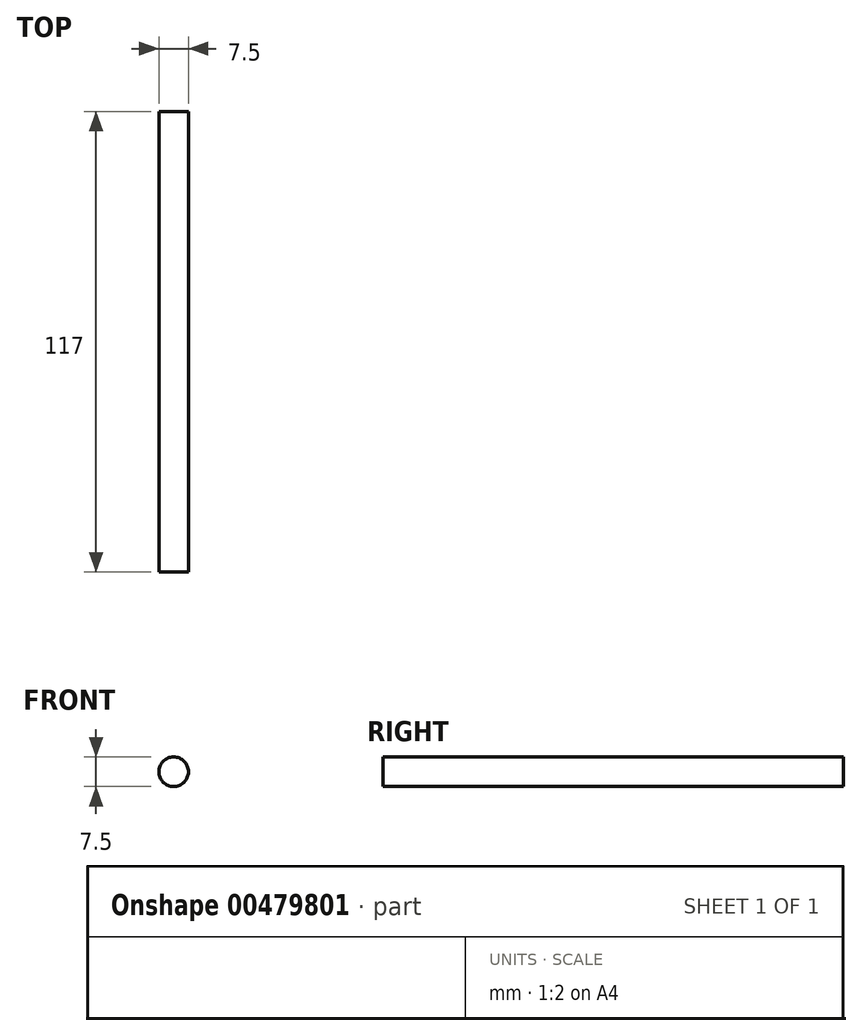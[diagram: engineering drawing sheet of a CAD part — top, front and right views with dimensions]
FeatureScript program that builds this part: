
annotation { "Feature Type Name" : "Feature", "Feature Type Description" : "" }
export const myFeature = defineFeature(function(context is Context, id is Id, definition is map)
    precondition{}
    {
        {
            var Q0;
            Q0=qCreatedBy(makeId("Front.planeOp"),FACE);
            var sketch = newSketch(context, id + "F0", { "sketchPlane" : qUnion([Q0])});
            skCircle(sketch, "E0", {"center": v(0, 0) * mm, "radius": 3.75 * mm});
            skSolve(sketch);
        }
        {
            var Q0;
            Q0=makeQuery(id+"F0.imprint","IMPRINT",FACE,{"disambiguationData":[TD([[makeQuery(id+"F0.imprint","IMPRINT",EDGE,{"derivedFrom":sQuery(id+"F0.wireOp",EDGE,"E0")}),1.0]])]});
            var Q1;
            Q1=sQuery(id+"F0.wireOp",EDGE,"E0");
            extrude(context, id + "F1", {"entities" : qUnion([Q0]), "surfaceEntities" : qUnion([Q1]), "depth" : 117 * mm});
        }
    });
